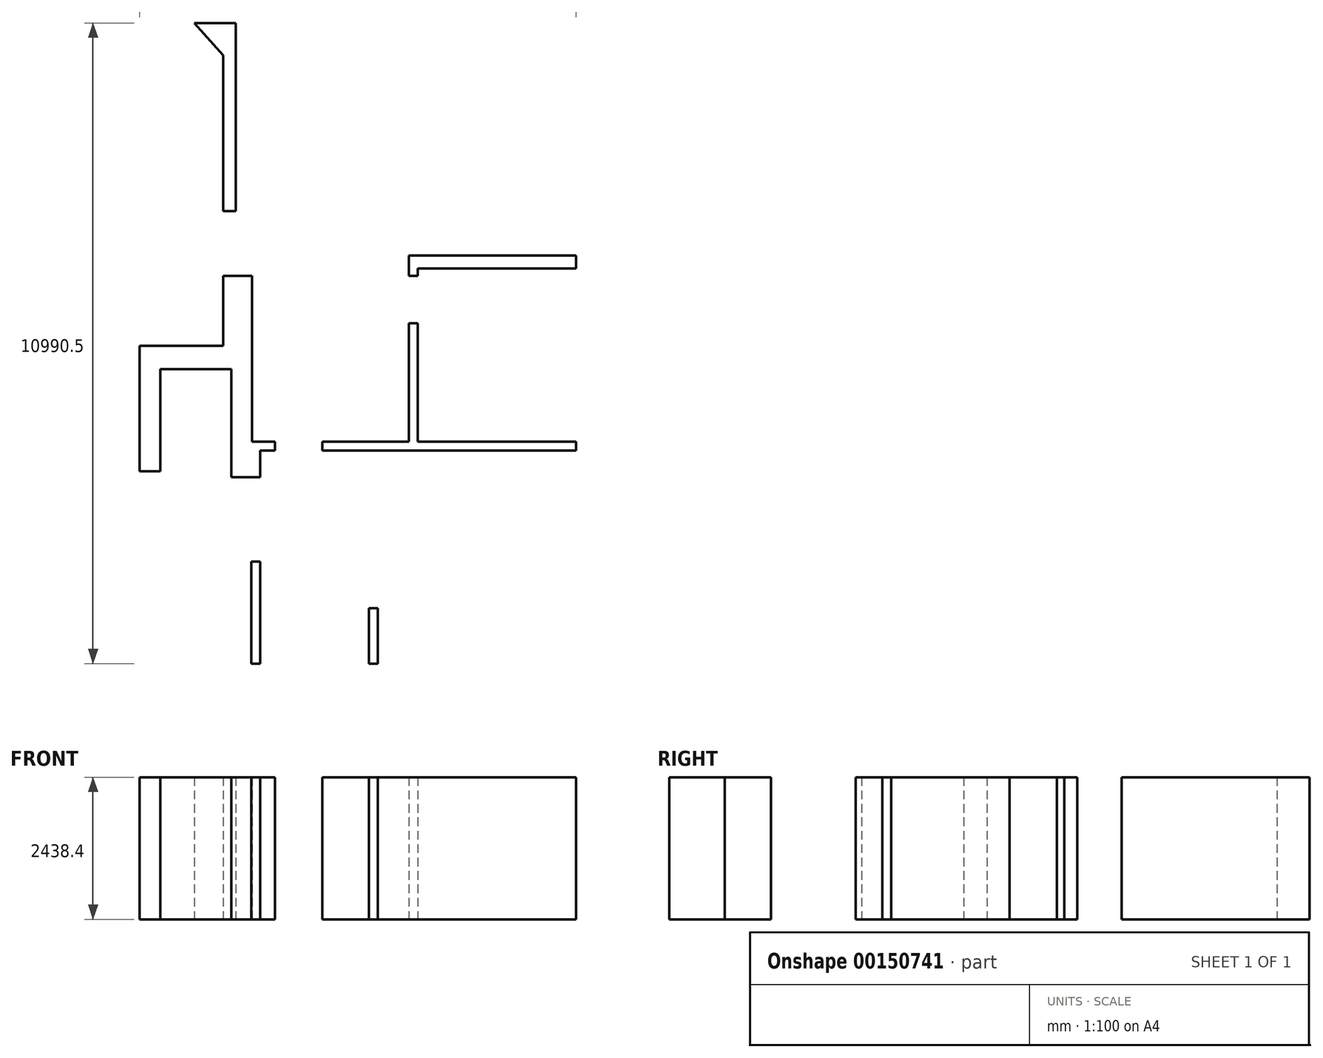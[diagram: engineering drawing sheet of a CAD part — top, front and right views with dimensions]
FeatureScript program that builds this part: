
annotation { "Feature Type Name" : "Feature", "Feature Type Description" : "" }
export const myFeature = defineFeature(function(context is Context, id is Id, definition is map)
    precondition{}
    {
        {
            var Q0;
            Q0=qCreatedBy(makeId("Top.planeOp"),FACE);
            var sketch = newSketch(context, id + "F0", { "sketchPlane" : qUnion([Q0])});
            skLineSegment(sketch, "E0.top", {"start": v(-1828.7, -2008.63) * mm, "end": v(1574.9, -2008.63) * mm});
            skLineSegment(sketch, "E0.left", {"start": v(-1828.7, -1058.26) * mm, "end": v(-1828.7, -2008.63) * mm});
            skLineSegment(sketch, "E0.right", {"start": v(1574.9, 1648.97) * mm, "end": v(1574.9, -2008.63) * mm});
            skLineSegment(sketch, "E1.top", {"start": v(-1981.1, -2008.63) * mm, "end": v(-3847.34, -2008.63) * mm});
            skLineSegment(sketch, "E1.left", {"start": v(-1981.1, -1058.26) * mm, "end": v(-1981.1, -2008.63) * mm});
            skLineSegment(sketch, "E1.right", {"start": v(-3847.34, 1648.97) * mm, "end": v(-3847.34, 1188.76) * mm});
            skLineSegment(sketch, "E2.bottom", {"start": v(-3999.74, -2008.63) * mm, "end": v(-9663.94, -2008.63) * mm});
            skLineSegment(sketch, "E2.left", {"start": v(-3999.74, -2008.63) * mm, "end": v(-3999.74, -261.74) * mm});
            skLineSegment(sketch, "E3.bottom", {"start": v(-1142.9, 1801.37) * mm, "end": v(1574.9, 1801.37) * mm});
            skLineSegment(sketch, "E3.top", {"start": v(-1142.9, 4773.17) * mm, "end": v(1574.9, 4773.17) * mm});
            skLineSegment(sketch, "E3.left", {"start": v(-1142.9, 1801.37) * mm, "end": v(-1142.9, 3833.37) * mm});
            skLineSegment(sketch, "E3.right", {"start": v(1574.9, 1801.37) * mm, "end": v(1574.9, 4773.17) * mm});
            skLineSegment(sketch, "E4.top", {"start": v(-3987.7, 1801.37) * mm, "end": v(-3594.17, 1801.37) * mm});
            skLineSegment(sketch, "E4.left", {"start": v(-3987.7, 4646.17) * mm, "end": v(-3987.7, 1801.37) * mm});
            skLineSegment(sketch, "E4.right", {"start": v(-1295.3, 3833.37) * mm, "end": v(-1295.3, 1801.37) * mm});
            skLineSegment(sketch, "E5.top", {"start": v(1574.9, 8981.86) * mm, "end": v(-4267.1, 8981.86) * mm});
            skLineSegment(sketch, "E5.left", {"start": v(1574.9, 4994.06) * mm, "end": v(1574.9, 8981.86) * mm});
            skLineSegment(sketch, "E6.top", {"start": v(-4343.3, 3045.97) * mm, "end": v(-5562.5, 3045.97) * mm});
            skLineSegment(sketch, "E6.left", {"start": v(-4343.3, 1191.77) * mm, "end": v(-4343.3, 3045.97) * mm});
            skLineSegment(sketch, "E6.right", {"start": v(-5562.5, 1293.37) * mm, "end": v(-5562.5, 3045.97) * mm});
            skLineSegment(sketch, "E7.trimOffspring", {"start": v(-5562.5, 1293.37) * mm, "end": v(-5918.1, 1293.37) * mm});
            skLineSegment(sketch, "E8.right", {"start": v(-5918.1, 1293.37) * mm, "end": v(-5918.1, 3045.97) * mm});
            skLineSegment(sketch, "E9", {"start": v(-9663.94, 3045.97) * mm, "end": v(-10012.83, 3394.85) * mm});
            skLineSegment(sketch, "E10", {"start": v(-10012.83, 3394.85) * mm, "end": v(-6366.6, 6633.55) * mm});
            skLineSegment(sketch, "E11", {"start": v(-6366.6, 6633.55) * mm, "end": v(-6920.8, 7257.48) * mm});
            skLineSegment(sketch, "E12", {"start": v(-6920.8, 7257.48) * mm, "end": v(-4979.44, 8981.86) * mm});
            skLineSegment(sketch, "E13", {"start": v(-4484.7, 8424.87) * mm, "end": v(-4484.7, 5930.26) * mm});
            skLineSegment(sketch, "E14", {"start": v(-4979.44, 8981.86) * mm, "end": v(-4484.7, 8424.87) * mm});
            skLineSegment(sketch, "E15", {"start": v(-9663.94, 3045.97) * mm, "end": v(-9663.94, -2008.63) * mm});
            skLineSegment(sketch, "E16", {"start": v(-5918.1, 3045.97) * mm, "end": v(-5918.1, 3442.42) * mm});
            skLineSegment(sketch, "E17", {"start": v(-1295.3, 4646.17) * mm, "end": v(-1142.9, 4646.17) * mm});
            skLineSegment(sketch, "E18", {"start": v(-1142.9, 3833.37) * mm, "end": v(-1295.3, 3833.37) * mm});
            skLineSegment(sketch, "E19.trimOffspring", {"start": v(-1142.9, 4646.17) * mm, "end": v(-1142.9, 4773.17) * mm});
            skLineSegment(sketch, "E20", {"start": v(-5918.1, 3442.42) * mm, "end": v(-4484.7, 3442.42) * mm});
            skLineSegment(sketch, "E21", {"start": v(-4267.1, 8981.86) * mm, "end": v(-4267.1, 5756.06) * mm});
            skLineSegment(sketch, "E22", {"start": v(-4267.1, 5756.06) * mm, "end": v(-4484.7, 5756.06) * mm});
            skLineSegment(sketch, "E23", {"start": v(-4484.7, 5756.06) * mm, "end": v(-4484.7, 5930.26) * mm});
            skLineSegment(sketch, "E24", {"start": v(-3594.17, 1801.37) * mm, "end": v(-3594.17, 1648.97) * mm});
            skLineSegment(sketch, "E25", {"start": v(-2781.37, 1648.97) * mm, "end": v(-2781.37, 1801.37) * mm});
            skLineSegment(sketch, "E26.trimOffspring", {"start": v(-2781.37, 1801.37) * mm, "end": v(-1295.3, 1801.37) * mm});
            skLineSegment(sketch, "E27.trimOffspring", {"start": v(-3594.17, 1648.97) * mm, "end": v(-3847.34, 1648.97) * mm});
            skLineSegment(sketch, "E28", {"start": v(-3999.74, -261.74) * mm, "end": v(-3847.34, -261.74) * mm});
            skLineSegment(sketch, "E29.trimOffspring", {"start": v(-3847.34, -261.74) * mm, "end": v(-3847.34, -2008.63) * mm});
            skLineSegment(sketch, "E30", {"start": v(-1981.1, -1058.26) * mm, "end": v(-1828.7, -1058.26) * mm});
            skLineSegment(sketch, "E31", {"start": v(-4484.7, 3442.42) * mm, "end": v(-4484.7, 4646.17) * mm});
            skLineSegment(sketch, "E32", {"start": v(-4484.7, 4646.17) * mm, "end": v(-3987.7, 4646.17) * mm});
            skLineSegment(sketch, "E33", {"start": v(-3999.74, -2008.63) * mm, "end": v(-3847.34, -2008.63) * mm});
            skLineSegment(sketch, "E34", {"start": v(-1981.1, -2008.63) * mm, "end": v(-1828.7, -2008.63) * mm});
            skLineSegment(sketch, "E35", {"start": v(1574.9, 1801.37) * mm, "end": v(1574.9, 1648.97) * mm});
            skLineSegment(sketch, "E36", {"start": v(-4979.44, 8981.86) * mm, "end": v(-4267.1, 8981.86) * mm});
            skLineSegment(sketch, "E37", {"start": v(1574.9, 4994.06) * mm, "end": v(1574.9, 4773.17) * mm});
            skLineSegment(sketch, "E38", {"start": v(-1295.3, 4646.17) * mm, "end": v(-1295.3, 4994.06) * mm});
            skLineSegment(sketch, "E39", {"start": v(-1295.3, 4994.06) * mm, "end": v(1574.9, 4994.06) * mm});
            skLineSegment(sketch, "E40", {"start": v(-2781.37, 1648.97) * mm, "end": v(1574.9, 1648.97) * mm});
            skLineSegment(sketch, "E41", {"start": v(-4343.3, 1191.77) * mm, "end": v(-3847.34, 1188.76) * mm});
            skSolve(sketch);
        }
        {
            var Q0;
            Q0=makeQuery(id+"F0.imprint","IMPRINT",FACE,{"disambiguationData":[TD([[makeQuery(id+"F0.imprint","IMPRINT",EDGE,{"derivedFrom":sQuery(id+"F0.wireOp",EDGE,"E1.right")}),-1.0]])]});
            var Q1;
            Q1=makeQuery(id+"F0.imprint","IMPRINT",FACE,{"disambiguationData":[TD([[makeQuery(id+"F0.imprint","IMPRINT",EDGE,{"derivedFrom":sQuery(id+"F0.wireOp",EDGE,"E13")}),1.0]])]});
            var Q2;
            Q2=makeQuery(id+"F0.imprint","IMPRINT",FACE,{"disambiguationData":[TD([[makeQuery(id+"F0.imprint","IMPRINT",EDGE,{"derivedFrom":sQuery(id+"F0.wireOp",EDGE,"E3.top")}),1.0]])]});
            var Q3;
            Q3=makeQuery(id+"F0.imprint","IMPRINT",FACE,{"disambiguationData":[TD([[makeQuery(id+"F0.imprint","IMPRINT",EDGE,{"derivedFrom":sQuery(id+"F0.wireOp",EDGE,"E3.bottom")}),-1.0]])]});
            var Q4;
            Q4=makeQuery(id+"F0.imprint","IMPRINT",FACE,{"disambiguationData":[TD([[makeQuery(id+"F0.imprint","IMPRINT",EDGE,{"derivedFrom":sQuery(id+"F0.wireOp",EDGE,"E0.left")}),-1.0]])]});
            var Q5;
            Q5=makeQuery(id+"F0.imprint","IMPRINT",FACE,{"disambiguationData":[TD([[makeQuery(id+"F0.imprint","IMPRINT",EDGE,{"derivedFrom":sQuery(id+"F0.wireOp",EDGE,"E2.left")}),-1.0]])]});
            extrude(context, id + "F1", {"entities" : qUnion([Q0, Q1, Q2, Q3, Q4, Q5]), "depth" : 2438.4 * mm});
        }
        {
            var Q0;
            Q0=sQuery(id+"F0.wireOp",EDGE,"E5.left");
            var Q1;
            Q1=sQuery(id+"F0.wireOp",EDGE,"E3.right");
            var Q2;
            Q2=sQuery(id+"F0.wireOp",EDGE,"E0.right");
            var Q3;
            Q3=sQuery(id+"F0.wireOp",EDGE,"E0.top");
            var Q4;
            Q4=sQuery(id+"F0.wireOp",EDGE,"E1.top");
            var Q5;
            Q5=sQuery(id+"F0.wireOp",EDGE,"E2.bottom");
            var Q6;
            Q6=sQuery(id+"F0.wireOp",EDGE,"E15");
            var Q7;
            Q7=sQuery(id+"F0.wireOp",EDGE,"E9");
            var Q8;
            Q8=sQuery(id+"F0.wireOp",EDGE,"E10");
            var Q9;
            Q9=sQuery(id+"F0.wireOp",EDGE,"E11");
            var Q10;
            Q10=sQuery(id+"F0.wireOp",EDGE,"E12");
            var Q11;
            Q11=sQuery(id+"F0.wireOp",EDGE,"E5.top");
            extrude(context, id + "F2", {"bodyType" : ToolBodyType.SURFACE, "surfaceEntities" : qUnion([Q0, Q1, Q2, Q3, Q4, Q5, Q6, Q7, Q8, Q9, Q10, Q11]), "depth" : 2438.4 * mm});
        }
    });
